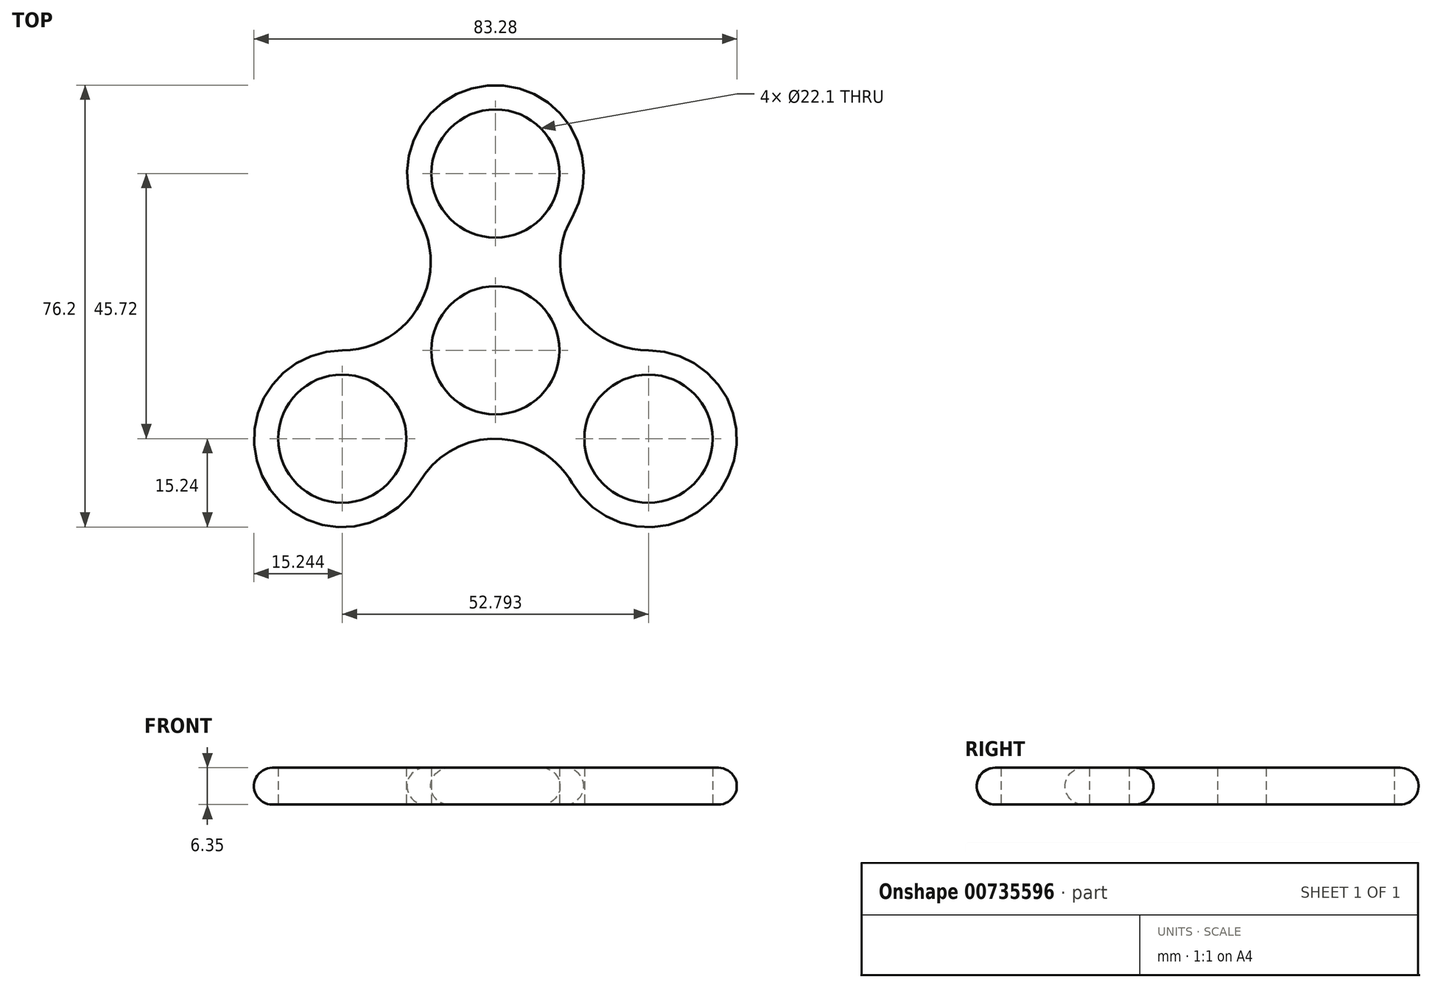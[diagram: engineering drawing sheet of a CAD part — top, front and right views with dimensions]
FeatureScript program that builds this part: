
annotation { "Feature Type Name" : "Feature", "Feature Type Description" : "" }
export const myFeature = defineFeature(function(context is Context, id is Id, definition is map)
    precondition{}
    {
        {
            var Q0;
            Q0=qCreatedBy(makeId("Top.planeOp"),FACE);
            var sketch = newSketch(context, id + "F0", { "sketchPlane" : qUnion([Q0])});
            skCircle(sketch, "E0", {"center": v(0, 0) * mm, "radius": 11.05 * mm});
            skLineSegment(sketch, "E1", {"start": v(0, 0) * mm, "end": v(0, 30.48) * mm});
            skCircle(sketch, "E2", {"center": v(0, 30.48) * mm, "radius": 11.05 * mm});
            skArc(sketch, "E3", {"start": v(13.2, 22.86) * mm, "mid": v(0, 45.72) * mm, "end": v(-13.2, 22.86) * mm});
            skArc(sketch, "E4.1.0", {"start": v(-26.4, 0) * mm, "mid": v(-39.6, -22.86) * mm, "end": v(-13.2, -22.86) * mm});
            skCircle(sketch, "E4.1.1", {"center": v(-26.4, -15.24) * mm, "radius": 11.05 * mm});
            skArc(sketch, "E4.2.0", {"start": v(13.2, -22.86) * mm, "mid": v(39.6, -22.86) * mm, "end": v(26.4, 0) * mm});
            skCircle(sketch, "E4.2.1", {"center": v(26.4, -15.24) * mm, "radius": 11.05 * mm});
            skLineSegment(sketch, "E5", {"start": v(0, 0) * mm, "end": v(-26.4, 15.24) * mm});
            skArc(sketch, "E6", {"start": v(-26.4, 0) * mm, "mid": v(-13.2, 7.62) * mm, "end": v(-13.2, 22.86) * mm});
            skArc(sketch, "E7.1.0", {"start": v(13.2, -22.86) * mm, "mid": v(0, -15.24) * mm, "end": v(-13.2, -22.86) * mm});
            skArc(sketch, "E7.2.0", {"start": v(13.2, 22.86) * mm, "mid": v(13.2, 7.62) * mm, "end": v(26.4, 0) * mm});
            skSolve(sketch);
        }
        {
            var Q0;
            Q0=makeQuery(id+"F0.imprint","IMPRINT",FACE,{"disambiguationData":[TD([[makeQuery(id+"F0.imprint","IMPRINT",EDGE,{"derivedFrom":sQuery(id+"F0.wireOp",EDGE,"E2")}),-1.0]])]});
            extrude(context, id + "F1", {"entities" : qUnion([Q0]), "depth" : 6.35 * mm, "offsetDistance" : 25.4 * mm});
        }
        {
            var Q0;
            Q0=makeQuery(id+"F1.opExtrude","CAP_EDGE",EDGE,{"disambiguationData":[OSD([sQuery(id+"F0.wireOp",EDGE,"E6")])],"isStart":false});
            var Q1;
            Q1=makeQuery(id+"F1.opExtrude","CAP_EDGE",EDGE,{"disambiguationData":[OSD([sQuery(id+"F0.wireOp",EDGE,"E3")])],"isStart":false});
            var Q2;
            Q2=makeQuery(id+"F1.opExtrude","CAP_EDGE",EDGE,{"disambiguationData":[OSD([sQuery(id+"F0.wireOp",EDGE,"E7.2.0")])],"isStart":false});
            var Q3;
            Q3=makeQuery(id+"F1.opExtrude","CAP_EDGE",EDGE,{"disambiguationData":[OSD([sQuery(id+"F0.wireOp",EDGE,"E4.2.0")])],"isStart":false});
            var Q4;
            Q4=makeQuery(id+"F1.opExtrude","CAP_EDGE",EDGE,{"disambiguationData":[OSD([sQuery(id+"F0.wireOp",EDGE,"E4.1.0")])],"isStart":false});
            var Q5;
            Q5=makeQuery(id+"F1.opExtrude","CAP_EDGE",EDGE,{"disambiguationData":[OSD([sQuery(id+"F0.wireOp",EDGE,"E7.1.0")])],"isStart":false});
            var Q6;
            Q6=makeQuery(id+"F1.opExtrude","CAP_EDGE",EDGE,{"disambiguationData":[OSD([sQuery(id+"F0.wireOp",EDGE,"E7.1.0")])],"isStart":true});
            var Q7;
            Q7=makeQuery(id+"F1.opExtrude","CAP_EDGE",EDGE,{"disambiguationData":[OSD([sQuery(id+"F0.wireOp",EDGE,"E6")])],"isStart":true});
            var Q8;
            Q8=makeQuery(id+"F1.opExtrude","CAP_EDGE",EDGE,{"disambiguationData":[OSD([sQuery(id+"F0.wireOp",EDGE,"E7.2.0")])],"isStart":true});
            var Q9;
            Q9=makeQuery(id+"F1.opExtrude","CAP_EDGE",EDGE,{"disambiguationData":[OSD([sQuery(id+"F0.wireOp",EDGE,"E4.2.0")])],"isStart":true});
            var Q10;
            Q10=makeQuery(id+"F1.opExtrude","CAP_EDGE",EDGE,{"disambiguationData":[OSD([sQuery(id+"F0.wireOp",EDGE,"E4.1.0")])],"isStart":true});
            fillet(context, id + "F2", {"entities" : qUnion([Q0, Q1, Q2, Q3, Q4, Q5, Q6, Q7, Q8, Q9, Q10]), "radius" : 3.17 * mm, "tangentPropagation" : true, "allowEdgeOverflow" : false});
        }
    });
